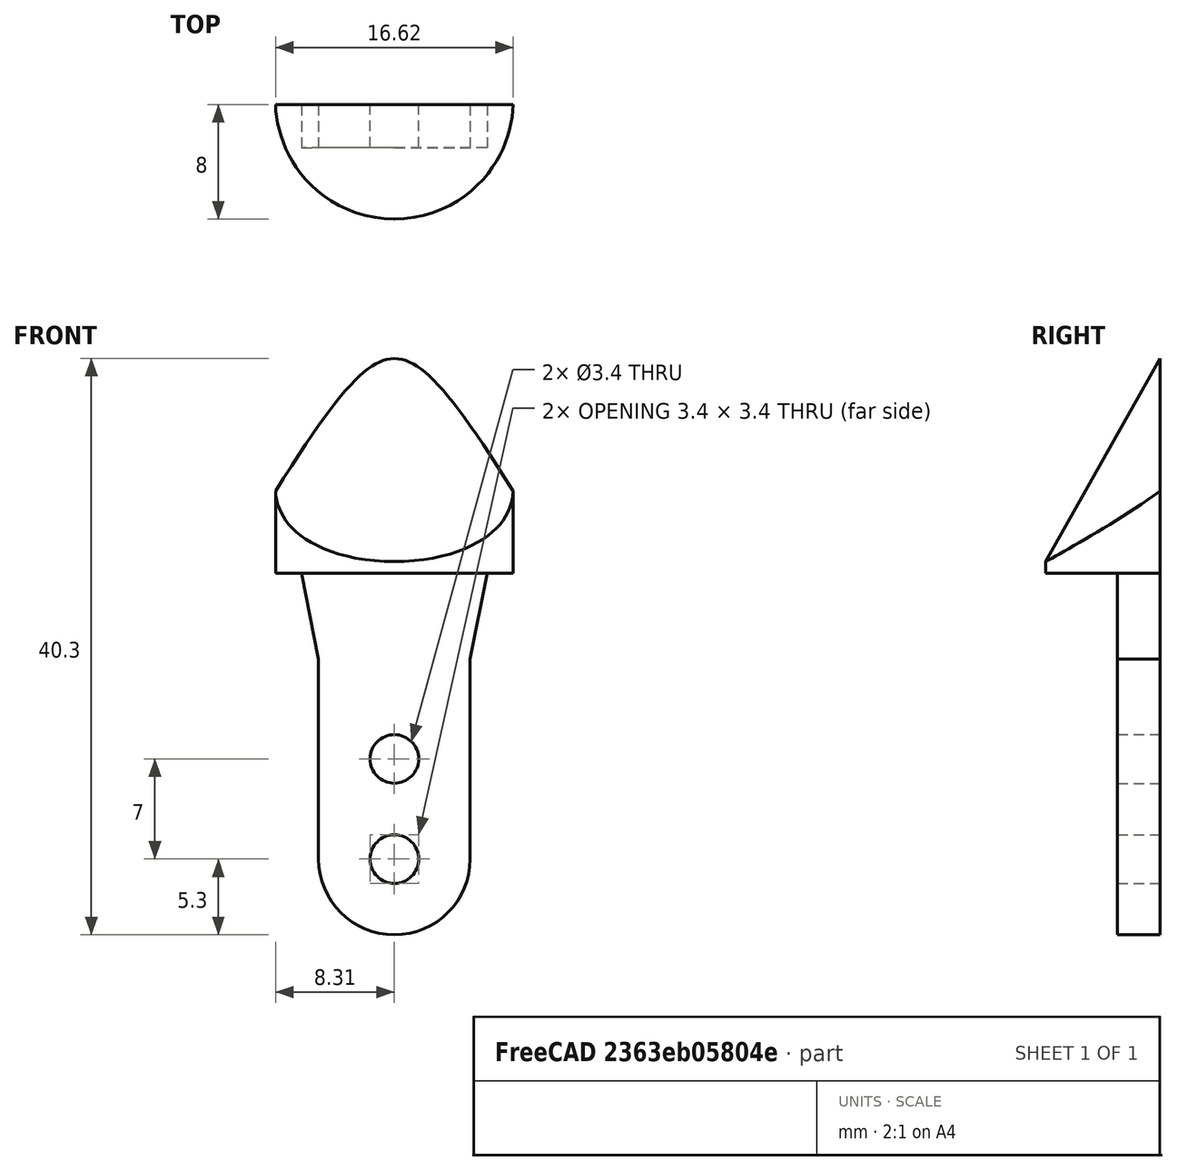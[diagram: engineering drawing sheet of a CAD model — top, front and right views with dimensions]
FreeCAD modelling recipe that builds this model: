
FCSTD DOCUMENT  (FreeCAD 0.21R31917 (Git))
Label: Зацеп3
License: All rights reserved
LicenseURL: http://en.wikipedia.org/wiki/All_rights_reserved
objects: Sketcher::SketchObject×6, PartDesign::Pocket×2, Mesh::Feature×1, PartDesign::Pad×1, PartDesign::Plane×1, PartDesign::Line×1, PartDesign::Revolution×1, PartDesign::Mirrored×1, PartDesign::Body×1
note: 18 computed .brp shape members not serialized (recipe doc carries the construction recipe); baked Part::Feature solids carry a one-line shape summary decoded from their .brp

FEATURE [Mesh::Feature] Zacep4
FEATURE [Sketcher::SketchObject] Sketch
  FullyConstrained = true
  MapMode = 5
  Placement = pos=(0,0,0) rot=(1,0,0;1.5708rad)
  Support = -> [XZ_Plane]
  sketch-geometry (9):
    g0: ArcOfCircle CenterX=0 CenterY=0 CenterZ=0 NormalX=0 NormalY=0 NormalZ=1 AngleXU=0 Radius=1.7 StartAngle=4.71239 EndAngle=7.85398
    g1: ArcOfCircle CenterX=0 CenterY=0 CenterZ=0 NormalX=0 NormalY=0 NormalZ=1 AngleXU=0 Radius=5.3 StartAngle=4.71239 EndAngle=6.28318
    g2: ArcOfCircle CenterX=0 CenterY=7 CenterZ=0 NormalX=0 NormalY=0 NormalZ=1 AngleXU=0 Radius=1.7 StartAngle=4.71239 EndAngle=7.85398
    g3: LineSegment StartX=-3e-16 StartY=5.3 StartZ=0 EndX=5e-16 EndY=1.7 EndZ=0
    g4: LineSegment StartX=5.3 StartY=-2.83485e-05 StartZ=0 EndX=5.3 EndY=14 EndZ=0
    g5: LineSegment StartX=5e-16 StartY=8.7 StartZ=0 EndX=5e-16 EndY=20 EndZ=0
    g6: LineSegment StartX=5e-16 StartY=20 StartZ=0 EndX=6.5 EndY=20 EndZ=0
    g7: LineSegment StartX=6.5 StartY=20 StartZ=0 EndX=5.3 EndY=14 EndZ=0
    g8: LineSegment StartX=-1e-15 StartY=-1.7 StartZ=0 EndX=-1e-15 EndY=-5.3 EndZ=0
  constraints (30):
    c: PointOnObject(g0,g-2)
    c: PointOnObject(g0,g-2)
    c: PointOnObject(g0,g-2)
    c: Coincident(g1,g0)
    c: Diameter(g1) = 10.6
    c: Diameter(g0) = 3.4
    c: PointOnObject(g2,g-2)
    c: PointOnObject(g2,g-2)
    c: Diameter(g2) = 3.4
    c: Distance(g0,g2) = 7
    c: Coincident(g3,g2)
    c: Coincident(g3,g0)
    c: Coincident(g4,g1)
    c: Vertical(g4)
    c: Coincident(g5,g2)
    c: PointOnObject(g5,g-2)
    c: Vertical(g5)
    c: Tangent(g4,g1)
    c: Coincident(g6,g5)
    c: Horizontal(g6)
    c: Coincident(g7,g6)
    c: Coincident(g7,g4)
    c: Distance(g4) = 14
    c: Coincident(g8,g0)
    c: Coincident(g8,g1)
    c: DistanceY(g2,g5) = 13
    c: PointOnObject(g0,g-1)
    c: Vertical(g8)
    c: DistanceX(g4,g6) = 1.2
    c: DistanceY(g5) = 20  'total_length'
FEATURE [PartDesign::Pad] Pad
  Direction = (0,-1,-2e-16)
  Length = 3
  Length2 = 100
  Placement = pos=(0,0,0) rot=(1,0,0;1.5708rad)
  Profile = -> Sketch
  Type = 0
FEATURE [Sketcher::SketchObject] Sketch001
  FullyConstrained = false
  MapMode = 5
  Support = -> [XY_Plane]
  sketch-geometry (3):
    g0: ArcOfCircle CenterX=0 CenterY=4 CenterZ=0 NormalX=0 NormalY=0 NormalZ=1 AngleXU=0 Radius=12.5 StartAngle=4.71239 EndAngle=5.75414
    g1: ArcOfCircle CenterX=0 CenterY=4 CenterZ=0 NormalX=0 NormalY=0 NormalZ=1 AngleXU=0 Radius=4 StartAngle=4.71239 EndAngle=5.76104
    g2: LineSegment StartX=3.467 StartY=2.00502 StartZ=0 EndX=10.7911 EndY=-2.30884 EndZ=0
  constraints (8):
    c: PointOnObject(g0,g-2)
    c: PointOnObject(g0,g-2)
    c: Diameter(g0) = 25
    c: Coincident(g1,g0)
    c: Coincident(g1,g-1)
    c: Coincident(g2,g1)
    c: Coincident(g2,g0)
    c: Diameter(g1) = 8
FEATURE [PartDesign::Plane] DatumPlane
  Length = 60
  MapMode = 5
  Placement = pos=(0,-4.4e-15,20) rot=(0,0,1;3.14159rad)
  ResizeMode = 0
  Support = -> [Pad]
  Width = 60
FEATURE [Sketcher::SketchObject] Sketch002
  FullyConstrained = true
  MapMode = 5
  Placement = pos=(0,-4.4e-15,20) rot=(0,0,1;3.14159rad)
  Support = -> [DatumPlane]
FEATURE [Sketcher::SketchObject] Sketch003
  FullyConstrained = true
  MapMode = 5
  Placement = pos=(0,0,0) rot=(0.57735,0.57735,0.57735;2.0944rad)
  Support = -> [YZ_Plane]
  expr: Constraints[8] = Sketch.Constraints.total_length
  sketch-geometry (4):
    g0: LineSegment StartX=0 StartY=35 StartZ=0 EndX=-8 EndY=20.8 EndZ=0
    g1: LineSegment StartX=-8 StartY=20.8 StartZ=0 EndX=-8 EndY=20 EndZ=0
    g2: LineSegment StartX=-8 StartY=20 StartZ=0 EndX=0 EndY=20 EndZ=0
    g3: LineSegment StartX=0 StartY=20 StartZ=0 EndX=0 EndY=35 EndZ=0
  constraints (12):
    c: PointOnObject(g0,g-2)
    c: Coincident(g1,g0)
    c: Vertical(g1)
    c: Coincident(g2,g1)
    c: PointOnObject(g2,g-2)
    c: Horizontal(g2)
    c: Coincident(g3,g2)
    c: Coincident(g3,g0)
    c: Distance(g2,g-1) = 20
    c: Distance(g1) = 0.8
    c: Distance(g3) = 15
    c: Distance(g2) = 8
FEATURE [PartDesign::Line] DatumLine
  AttacherType = Attacher::AttachEngineLine
  Length = 20
  MapMode = 19
  Placement = pos=(0,4,0) rot=(0,0,1;4.71239rad)
  ResizeMode = 0
  Support = -> [Sketch001]
FEATURE [PartDesign::Revolution] Revolution
  Angle = 90
  Axis = (-1e-16,-1e-16,1)
  Base = (0,4,0)
  BaseFeature = -> Pad
  Placement = pos=(0,0,0) rot=(1,0,0;1.5708rad)
  Profile = -> Sketch003
  ReferenceAxis = -> DatumLine
FEATURE [Sketcher::SketchObject] Sketch004
  FullyConstrained = false
  MapMode = 5
  Support = -> [XY_Plane]
  sketch-geometry (4):
    g0: LineSegment StartX=0 StartY=0 StartZ=0 EndX=30.0652 EndY=0 EndZ=0
    g1: LineSegment StartX=30.0652 StartY=0 StartZ=0 EndX=30.0652 EndY=28.066 EndZ=0
    g2: LineSegment StartX=30.0652 StartY=28.066 StartZ=0 EndX=0 EndY=28.066 EndZ=0
    g3: LineSegment StartX=0 StartY=28.066 StartZ=0 EndX=0 EndY=0 EndZ=0
  constraints (9):
    c: Coincident(g0,g1)
    c: Coincident(g1,g2)
    c: Coincident(g2,g3)
    c: Coincident(g3,g0)
    c: Horizontal(g0)
    c: Horizontal(g2)
    c: Vertical(g1)
    c: Vertical(g3)
    c: Coincident(g0,g-1)
FEATURE [PartDesign::Pocket] Pocket
  BaseFeature = -> Revolution
  Direction = (0,0,-1)
  Length = 5
  Length2 = 100
  Midplane = true
  Placement = pos=(0,0,0) rot=(1,0,0;1.5708rad)
  Profile = -> Sketch004
  Type = 1
FEATURE [Sketcher::SketchObject] Sketch005
  FullyConstrained = false
  MapMode = 5
  Support = -> [XY_Plane]
  sketch-geometry (3):
    g0: ArcOfCircle CenterX=0 CenterY=0.319859 CenterZ=0 NormalX=0 NormalY=0 NormalZ=1 AngleXU=0 Radius=8.31986 StartAngle=4.71239 EndAngle=6.24473
    g1: LineSegment StartX=8.31371 StartY=-3.2e-15 StartZ=0 EndX=11.3137 EndY=7.1e-15 EndZ=0
    g2: ArcOfCircle CenterX=-1.9e-15 CenterY=4 CenterZ=0 NormalX=0 NormalY=0 NormalZ=1 AngleXU=0 Radius=12 StartAngle=4.71239 EndAngle=5.94335
  constraints (8):
    c: PointOnObject(g0,g-2)
    c: PointOnObject(g0,g-1)
    c: Coincident(g1,g0)
    c: Coincident(g2,g1)
    c: Coincident(g2,g0)
    c: Diameter(g2) = 24
    c: Diameter(g0) = 16.6397
    c: Distance(g1) = 3
FEATURE [PartDesign::Pocket] Pocket001
  BaseFeature = -> Pocket
  Direction = (0,0,-1)
  Length = 5
  Length2 = 100
  Placement = pos=(0,0,0) rot=(1,0,0;1.5708rad)
  Profile = -> Sketch005
  Reversed = true
  Type = 1
FEATURE [PartDesign::Mirrored] Mirrored
  BaseFeature = -> Pocket001
  MirrorPlane = -> Sketch [V_Axis]
  Originals = -> [Pad,Revolution,Pocket,Pocket001]
  Placement = pos=(0,0,0) rot=(1,0,0;1.5708rad)
  Refine = true
FEATURE [PartDesign::Body] Body
  Group = -> [Sketch,Pad,Sketch001,DatumPlane,Sketch002,Sketch003,DatumLine,Revolution,Sketch004,Pocket,Sketch005,Pocket001,Mirrored]
  Origin = -> Origin
  Tip = -> Mirrored
